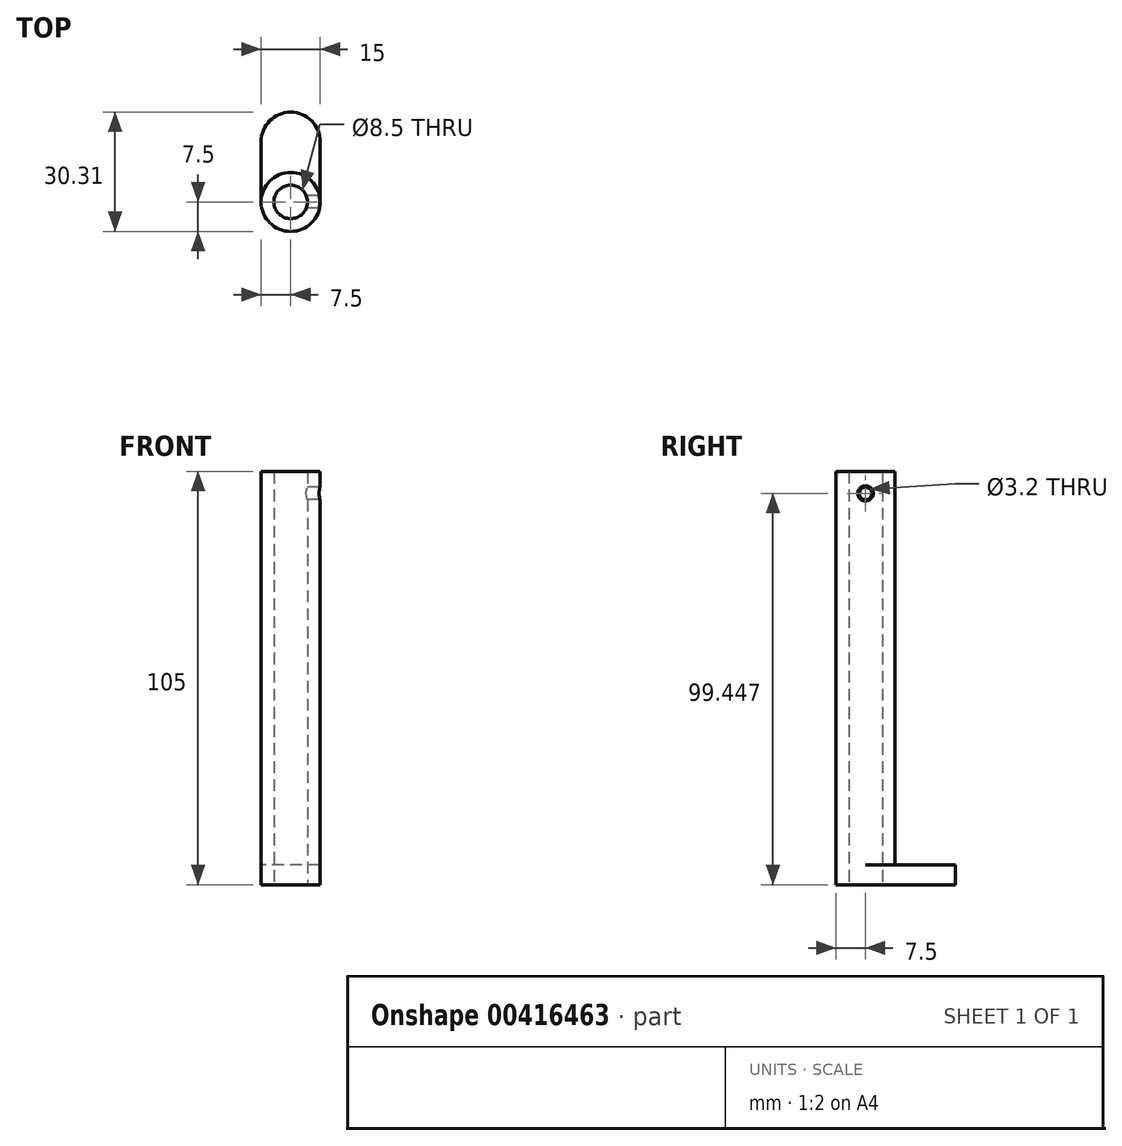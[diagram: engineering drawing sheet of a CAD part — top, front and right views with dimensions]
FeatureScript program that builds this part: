
annotation { "Feature Type Name" : "Feature", "Feature Type Description" : "" }
export const myFeature = defineFeature(function(context is Context, id is Id, definition is map)
    precondition{}
    {
        {
            var Q0;
            Q0=qCreatedBy(makeId("Top.planeOp"),FACE);
            var sketch = newSketch(context, id + "F0", { "sketchPlane" : qUnion([Q0])});
            skCircle(sketch, "E0", {"center": v(0, 0) * mm, "radius": 4.25 * mm});
            skCircle(sketch, "E1", {"center": v(0, 0) * mm, "radius": 7.5 * mm});
            skSolve(sketch);
        }
        {
            var Q0;
            Q0=makeQuery(id+"F0.imprint","IMPRINT",FACE,{"disambiguationData":[TD([[makeQuery(id+"F0.imprint","IMPRINT",EDGE,{"derivedFrom":sQuery(id+"F0.wireOp",EDGE,"E0")}),-1.0]])]});
            var Q1;
            Q1 = qSketchRegion(id + "F2", true);
            extrude(context, id + "F1", {"entities" : qUnion([Q0, Q1]), "depth" : 100 * mm});
        }
        {
            var Q0;
            Q0=qCreatedBy(makeId("Top.planeOp"),FACE);
            var sketch = newSketch(context, id + "F2", { "sketchPlane" : qUnion([Q0])});
            skLineSegment(sketch, "E2.bottom", {"start": v(-7.5, 0) * mm, "end": v(7.5, 0) * mm});
            skLineSegment(sketch, "E2.top", {"start": v(-7.5, 15.3) * mm, "end": v(7.5, 15.3) * mm});
            skLineSegment(sketch, "E2.left", {"start": v(-7.5, 0) * mm, "end": v(-7.5, 15.3) * mm});
            skLineSegment(sketch, "E2.right", {"start": v(7.5, 0) * mm, "end": v(7.5, 15.3) * mm});
            skArc(sketch, "E3", {"start": v(-7.5, 15.3) * mm, "mid": v(0, 22.8) * mm, "end": v(7.5, 15.3) * mm});
            skCircle(sketch, "E4", {"center": v(0, 0) * mm, "radius": 4.25 * mm});
            skCircle(sketch, "E5", {"center": v(0, 0) * mm, "radius": 7.5 * mm});
            skSolve(sketch);
        }
        {
            var Q0;
            Q0 = qSketchRegion(id + "F2", true);
            extrude(context, id + "F3", {"entities" : qUnion([Q0]), "operationType" : NewBodyOperationType.ADD, "oppositeDirection" : true, "depth" : 5 * mm});
        }
        {
            var Q0;
            Q0=qCreatedBy(makeId("Right.planeOp"),FACE);
            var sketch = newSketch(context, id + "F4", { "sketchPlane" : qUnion([Q0])});
            skCircle(sketch, "E6", {"center": v(0, 94.45) * mm, "radius": 1.6 * mm});
            skSolve(sketch);
        }
        {
            var Q0;
            Q0 = qSketchRegion(id + "F4", true);
            extrude(context, id + "F5", {"entities" : qUnion([Q0]), "operationType" : NewBodyOperationType.REMOVE, "depth" : 25 * mm});
        }
        {
            var Q0;
            Q0=makeQuery(id+"F5.boolean.opBoolean","INTERSECT",EDGE,{"derivedFrom":[makeQuery(id+"F3.boolean.opBoolean","MERGE",FACE,{"derivedFrom":[makeQuery(id+"F1.opExtrude","SWEPT_FACE",FACE,{"disambiguationData":[OSD([sQuery(id+"F0.wireOp",EDGE,"E1")])]}),makeQuery(id+"F3.opExtrude","SWEPT_FACE",FACE,{"disambiguationData":[OSD([sQuery(id+"F2.wireOp",EDGE,"E5")])]})]}),makeQuery(id+"F5.opExtrude","SWEPT_FACE",FACE,{"disambiguationData":[OSD([sQuery(id+"F4.wireOp",EDGE,"E6")])]})]});
            chamfer(context, id + "F6", {"entities" : qUnion([Q0]), "width" : .3 * mm, "tangentPropagation" : true});
        }
    });
